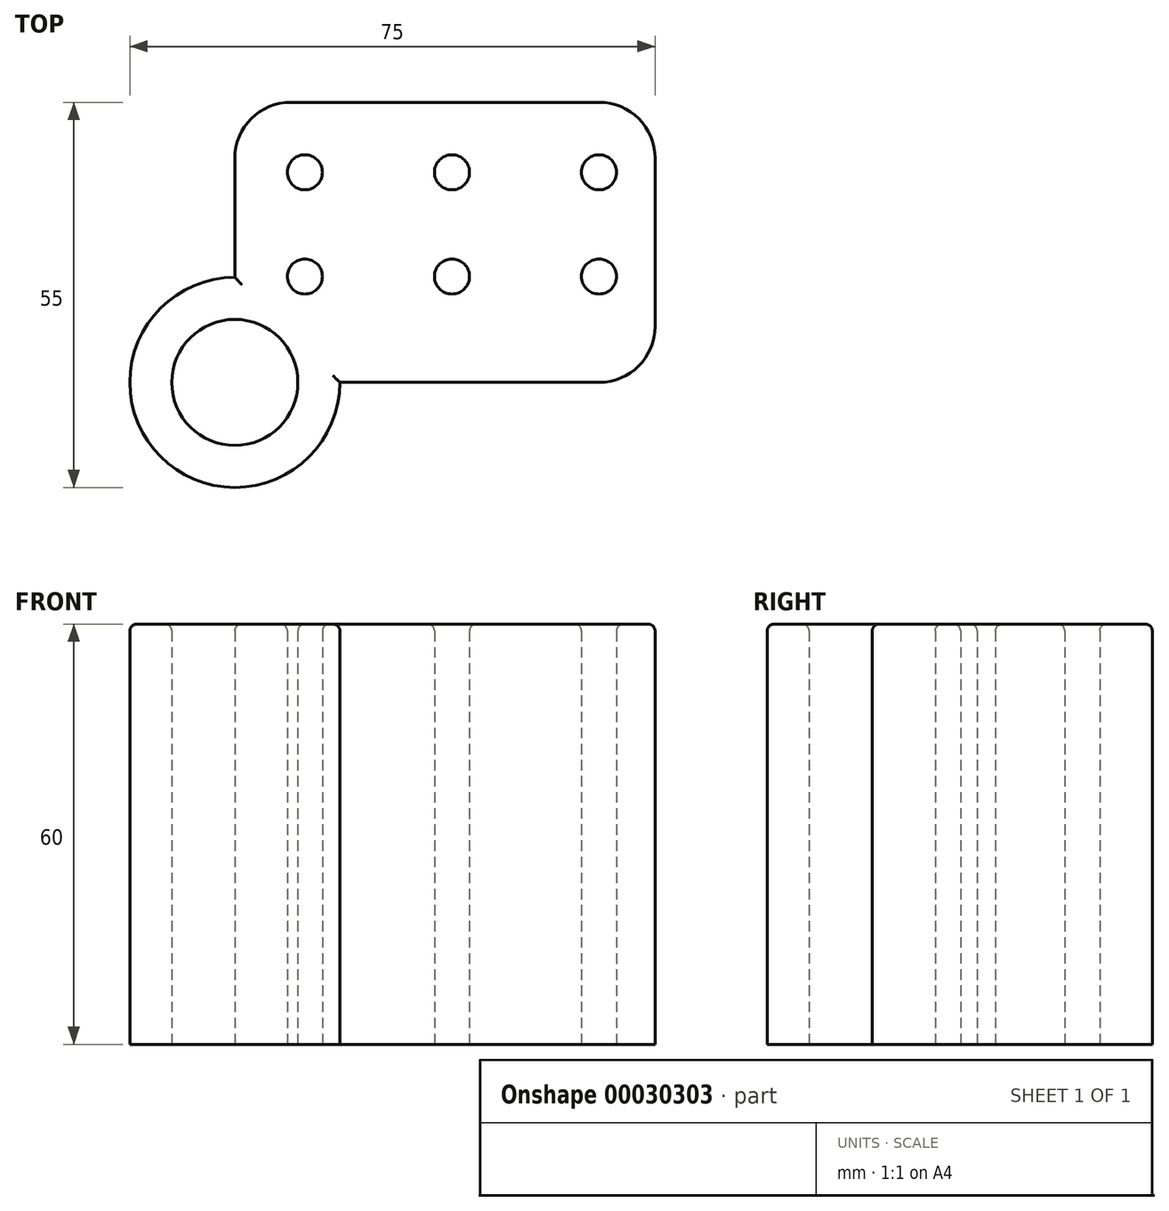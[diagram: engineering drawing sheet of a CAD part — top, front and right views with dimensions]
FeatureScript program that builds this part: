
annotation { "Feature Type Name" : "Feature", "Feature Type Description" : "" }
export const myFeature = defineFeature(function(context is Context, id is Id, definition is map)
    precondition{}
    {
        {
            var Q0;
            Q0=qCreatedBy(makeId("Top.planeOp"),FACE);
            var sketch = newSketch(context, id + "F0", { "sketchPlane" : qUnion([Q0])});
            skLineSegment(sketch, "E0.bottom", {"start": v(15, 0) * mm, "end": v(52, 0) * mm});
            skLineSegment(sketch, "E0.top", {"start": v(8, 40) * mm, "end": v(52, 40) * mm});
            skLineSegment(sketch, "E0.left", {"start": v(0, 15) * mm, "end": v(0, 32) * mm});
            skLineSegment(sketch, "E0.right", {"start": v(60, 8) * mm, "end": v(60, 32) * mm});
            skArc(sketch, "E1", {"start": v(0, 15) * mm, "mid": v(-10.6, -10.6) * mm, "end": v(15, 0) * mm});
            skCircle(sketch, "E2", {"center": v(0, 0) * mm, "radius": 9 * mm});
            skPoint(sketch, "E3.visualSharp", {"position": v(0, 40) * mm});
            skArc(sketch, "E3.filletArc", {"start": v(8, 40) * mm, "mid": v(2.34, 37.66) * mm, "end": v(0, 32) * mm});
            skPoint(sketch, "E4.visualSharp", {"position": v(60, 40) * mm});
            skArc(sketch, "E4.filletArc", {"start": v(60, 32) * mm, "mid": v(57.66, 37.66) * mm, "end": v(52, 40) * mm});
            skPoint(sketch, "E5.visualSharp", {"position": v(60, 0) * mm});
            skArc(sketch, "E5.filletArc", {"start": v(52, 0) * mm, "mid": v(57.66, 2.34) * mm, "end": v(60, 8) * mm});
            skCircle(sketch, "E6", {"center": v(10, 30) * mm, "radius": 2.5 * mm});
            skCircle(sketch, "E7.0.1.0", {"center": v(10, 15.12) * mm, "radius": 2.5 * mm});
            skLineSegment(sketch, "E7.0.1.1", {"start": v(8, 25.12) * mm, "end": v(52, 25.12) * mm});
            skLineSegment(sketch, "E7.0.1.2", {"start": v(0, 0.12) * mm, "end": v(0, 17.12) * mm});
            skCircle(sketch, "E7.1.0.0", {"center": v(31, 30) * mm, "radius": 2.5 * mm});
            skLineSegment(sketch, "E7.1.0.1", {"start": v(29, 40) * mm, "end": v(73, 40) * mm});
            skLineSegment(sketch, "E7.1.0.2", {"start": v(21, 15) * mm, "end": v(21, 32) * mm});
            skCircle(sketch, "E7.1.1.0", {"center": v(31, 15.12) * mm, "radius": 2.5 * mm});
            skLineSegment(sketch, "E7.1.1.1", {"start": v(29, 25.12) * mm, "end": v(73, 25.12) * mm});
            skLineSegment(sketch, "E7.1.1.2", {"start": v(21, 0.12) * mm, "end": v(21, 17.12) * mm});
            skCircle(sketch, "E7.2.0.0", {"center": v(52, 30) * mm, "radius": 2.5 * mm});
            skLineSegment(sketch, "E7.2.0.1", {"start": v(50, 40) * mm, "end": v(94, 40) * mm});
            skLineSegment(sketch, "E7.2.0.2", {"start": v(42, 15) * mm, "end": v(42, 32) * mm});
            skCircle(sketch, "E7.2.1.0", {"center": v(52, 15.12) * mm, "radius": 2.5 * mm});
            skLineSegment(sketch, "E7.2.1.1", {"start": v(50, 25.12) * mm, "end": v(94, 25.12) * mm});
            skLineSegment(sketch, "E7.2.1.2", {"start": v(42, 0.12) * mm, "end": v(42, 17.12) * mm});
            skLineSegment(sketch, "E7.direction1", {"start": v(10, 30) * mm, "end": v(31, 30) * mm, "construction": true});
            skLineSegment(sketch, "E7.direction2", {"start": v(10, 30) * mm, "end": v(10, 15.12) * mm, "construction": true});
            skSolve(sketch);
        }
        {
            var Q0;
            Q0=makeQuery(id+"F0.imprint","IMPRINT",FACE,{"disambiguationData":[TD([[makeQuery(id+"F0.imprint","IMPRINT",EDGE,{"derivedFrom":sQuery(id+"F0.wireOp",EDGE,"E0.bottom")}),1.0]])]});
            extrude(context, id + "F1", {"entities" : qUnion([Q0]), "depth" : 60 * mm});
        }
        {
            var Q0;
            Q0=makeQuery(id+"F1.opExtrude","CAP_FACE",FACE,{"disambiguationData":[OSD([sQuery(id+"F0.wireOp",EDGE,"E0.bottom"),sQuery(id+"F0.wireOp",EDGE,"E0.top"),sQuery(id+"F0.wireOp",EDGE,"E0.left"),sQuery(id+"F0.wireOp",EDGE,"E0.right"),sQuery(id+"F0.wireOp",EDGE,"E1"),sQuery(id+"F0.wireOp",EDGE,"E2"),sQuery(id+"F0.wireOp",EDGE,"E3.filletArc"),sQuery(id+"F0.wireOp",EDGE,"E4.filletArc"),sQuery(id+"F0.wireOp",EDGE,"E5.filletArc"),sQuery(id+"F0.wireOp",EDGE,"E6"),sQuery(id+"F0.wireOp",EDGE,"E7.0.1.0"),sQuery(id+"F0.wireOp",EDGE,"E7.0.1.2"),sQuery(id+"F0.wireOp",EDGE,"E7.1.0.0"),sQuery(id+"F0.wireOp",EDGE,"E7.1.0.1"),sQuery(id+"F0.wireOp",EDGE,"E7.1.1.0"),sQuery(id+"F0.wireOp",EDGE,"E7.2.0.0"),sQuery(id+"F0.wireOp",EDGE,"E7.2.0.1"),sQuery(id+"F0.wireOp",EDGE,"E7.2.1.0")])],"isStart":false});
            fillet(context, id + "F2", {"entities" : qUnion([Q0]), "radius" : 1 * mm, "tangentPropagation" : true, "allowEdgeOverflow" : false});
        }
    });
